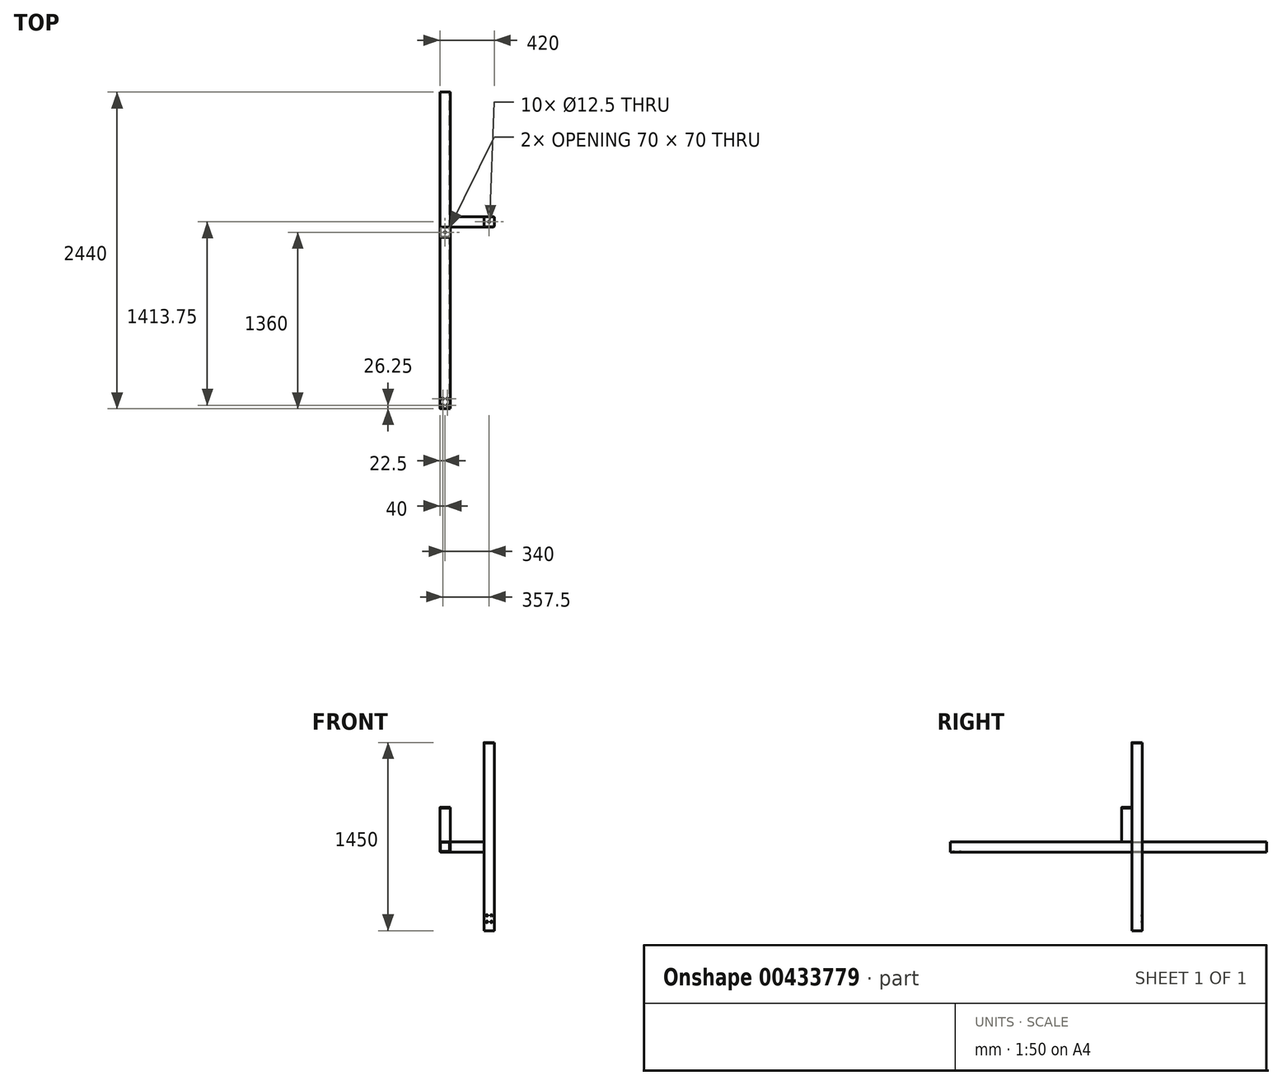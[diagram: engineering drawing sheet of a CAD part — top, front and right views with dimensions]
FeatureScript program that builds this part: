
annotation { "Feature Type Name" : "Feature", "Feature Type Description" : "" }
export const myFeature = defineFeature(function(context is Context, id is Id, definition is map)
    precondition{}
    {
        {
            var Q0;
            Q0=qCreatedBy(makeId("Top.planeOp"),FACE);
            var sketch = newSketch(context, id + "F0", { "sketchPlane" : qUnion([Q0])});
            skLineSegment(sketch, "E0.bottom", {"start": v(30, 40) * mm, "end": v(-30, 40) * mm});
            skLineSegment(sketch, "E0.top", {"start": v(30, -40) * mm, "end": v(-30, -40) * mm});
            skLineSegment(sketch, "E0.left", {"start": v(40, 30) * mm, "end": v(40, -30) * mm});
            skLineSegment(sketch, "E0.right", {"start": v(-40, 30) * mm, "end": v(-40, -30) * mm});
            skPoint(sketch, "E0.middle", {"position": v(0, 0) * mm});
            skPoint(sketch, "E1.visualSharp", {"position": v(-40, 40) * mm});
            skArc(sketch, "E1.filletArc", {"start": v(-30, 40) * mm, "mid": v(-37.07, 37.07) * mm, "end": v(-40, 30) * mm});
            skPoint(sketch, "E2.visualSharp", {"position": v(40, 40) * mm});
            skArc(sketch, "E2.filletArc", {"start": v(40, 30) * mm, "mid": v(37.07, 37.07) * mm, "end": v(30, 40) * mm});
            skPoint(sketch, "E3.visualSharp", {"position": v(40, -40) * mm});
            skArc(sketch, "E3.filletArc", {"start": v(30, -40) * mm, "mid": v(37.07, -37.07) * mm, "end": v(40, -30) * mm});
            skPoint(sketch, "E4.visualSharp", {"position": v(-40, -40) * mm});
            skArc(sketch, "E4.filletArc", {"start": v(-40, -30) * mm, "mid": v(-37.07, -37.07) * mm, "end": v(-30, -40) * mm});
            skArc(sketch, "E5.0", {"start": v(35, 30) * mm, "mid": v(33.54, 33.54) * mm, "end": v(30, 35) * mm});
            skLineSegment(sketch, "E5.1", {"start": v(35, 30) * mm, "end": v(35, -30) * mm});
            skLineSegment(sketch, "E5.2", {"start": v(30, 35) * mm, "end": v(-30, 35) * mm});
            skArc(sketch, "E5.3", {"start": v(30, -35) * mm, "mid": v(33.54, -33.54) * mm, "end": v(35, -30) * mm});
            skArc(sketch, "E5.4", {"start": v(-30, 35) * mm, "mid": v(-33.54, 33.54) * mm, "end": v(-35, 30) * mm});
            skLineSegment(sketch, "E5.5", {"start": v(-35, 30) * mm, "end": v(-35, -30) * mm});
            skArc(sketch, "E5.6", {"start": v(-35, -30) * mm, "mid": v(-33.54, -33.54) * mm, "end": v(-30, -35) * mm});
            skLineSegment(sketch, "E5.7", {"start": v(30, -35) * mm, "end": v(-30, -35) * mm});
            skSolve(sketch);
        }
        {
            var Q0;
            Q0=makeQuery(id+"F0.imprint","IMPRINT",FACE,{"disambiguationData":[TD([[makeQuery(id+"F0.imprint","IMPRINT",EDGE,{"derivedFrom":sQuery(id+"F0.wireOp",EDGE,"E0.bottom")}),1.0]])]});
            var Q1;
            Q1 = qConstructionFilter(qBodyType(qCreatedBy(id + "F0" ,EDGE), BodyType.WIRE), ConstructionObject.NO);
            extrude(context, id + "F1", {"entities" : qUnion([Q0]), "surfaceEntities" : qUnion([Q1]), "depth" : 1445 * mm});
        }
        {
            var Q0;
            Q0=makeQuery(id+"F1.opExtrude","SWEPT_FACE",FACE,{"disambiguationData":[OSD([sQuery(id+"F0.wireOp",EDGE,"E0.right")])]});
            var sketch = newSketch(context, id + "F2", { "sketchPlane" : qUnion([Q0])});
            skLineSegment(sketch, "E6", {"start": v(0, 1445) * mm, "end": v(0, 0) * mm, "construction": true});
            skLineSegment(sketch, "E7.bottom", {"start": v(30, 685) * mm, "end": v(-30, 685) * mm});
            skLineSegment(sketch, "E7.top", {"start": v(30, 605) * mm, "end": v(-30, 605) * mm});
            skLineSegment(sketch, "E7.left", {"start": v(40, 675) * mm, "end": v(40, 615) * mm});
            skLineSegment(sketch, "E7.right", {"start": v(-40, 675) * mm, "end": v(-40, 615) * mm});
            skPoint(sketch, "E7.middle", {"position": v(0, 645) * mm});
            skPoint(sketch, "E8.visualSharp", {"position": v(-40, 685) * mm});
            skArc(sketch, "E8.filletArc", {"start": v(-30, 685) * mm, "mid": v(-37.07, 682.07) * mm, "end": v(-40, 675) * mm});
            skPoint(sketch, "E9.visualSharp", {"position": v(40, 685) * mm});
            skArc(sketch, "E9.filletArc", {"start": v(40, 675) * mm, "mid": v(37.07, 682.07) * mm, "end": v(30, 685) * mm});
            skPoint(sketch, "E10.visualSharp", {"position": v(40, 605) * mm});
            skArc(sketch, "E10.filletArc", {"start": v(30, 605) * mm, "mid": v(37.07, 607.93) * mm, "end": v(40, 615) * mm});
            skPoint(sketch, "E11.visualSharp", {"position": v(-40, 605) * mm});
            skArc(sketch, "E11.filletArc", {"start": v(-40, 615) * mm, "mid": v(-37.07, 607.93) * mm, "end": v(-30, 605) * mm});
            skArc(sketch, "E12.0", {"start": v(35, 675) * mm, "mid": v(33.54, 678.54) * mm, "end": v(30, 680) * mm});
            skLineSegment(sketch, "E12.1", {"start": v(35, 675) * mm, "end": v(35, 615) * mm});
            skLineSegment(sketch, "E12.2", {"start": v(30, 680) * mm, "end": v(-30, 680) * mm});
            skArc(sketch, "E12.3", {"start": v(30, 610) * mm, "mid": v(33.54, 611.46) * mm, "end": v(35, 615) * mm});
            skArc(sketch, "E12.4", {"start": v(-30, 680) * mm, "mid": v(-33.54, 678.54) * mm, "end": v(-35, 675) * mm});
            skLineSegment(sketch, "E12.5", {"start": v(-35, 675) * mm, "end": v(-35, 615) * mm});
            skArc(sketch, "E12.6", {"start": v(-35, 615) * mm, "mid": v(-33.54, 611.46) * mm, "end": v(-30, 610) * mm});
            skLineSegment(sketch, "E12.7", {"start": v(30, 610) * mm, "end": v(-30, 610) * mm});
            skSolve(sketch);
        }
        {
            var Q0;
            Q0 = qSketchRegion(id + "F2", true);
            extrude(context, id + "F3", {"entities" : qUnion([Q0]), "depth" : 260 * mm});
        }
        {
            var Q0;
            Q0=qCreatedBy(makeId("Front.planeOp"),FACE);
            var sketch = newSketch(context, id + "F4", { "sketchPlane" : qUnion([Q0])});
            skLineSegment(sketch, "E13.bottom", {"start": v(-370, 685) * mm, "end": v(-310, 685) * mm});
            skLineSegment(sketch, "E13.top", {"start": v(-370, 605) * mm, "end": v(-310, 605) * mm});
            skLineSegment(sketch, "E13.left", {"start": v(-380, 675) * mm, "end": v(-380, 615) * mm});
            skLineSegment(sketch, "E13.right", {"start": v(-300, 675) * mm, "end": v(-300, 615) * mm});
            skPoint(sketch, "E13.middle", {"position": v(-340, 645) * mm});
            skPoint(sketch, "E14.visualSharp", {"position": v(-300, 685) * mm});
            skArc(sketch, "E14.filletArc", {"start": v(-300, 675) * mm, "mid": v(-302.93, 682.07) * mm, "end": v(-310, 685) * mm});
            skPoint(sketch, "E15.visualSharp", {"position": v(-380, 685) * mm});
            skArc(sketch, "E15.filletArc", {"start": v(-370, 685) * mm, "mid": v(-377.07, 682.07) * mm, "end": v(-380, 675) * mm});
            skPoint(sketch, "E16.visualSharp", {"position": v(-380, 605) * mm});
            skArc(sketch, "E16.filletArc", {"start": v(-380, 615) * mm, "mid": v(-377.07, 607.93) * mm, "end": v(-370, 605) * mm});
            skPoint(sketch, "E17.visualSharp", {"position": v(-300, 605) * mm});
            skArc(sketch, "E17.filletArc", {"start": v(-310, 605) * mm, "mid": v(-302.93, 607.93) * mm, "end": v(-300, 615) * mm});
            skArc(sketch, "E18.0", {"start": v(-370, 680) * mm, "mid": v(-373.54, 678.54) * mm, "end": v(-375, 675) * mm});
            skLineSegment(sketch, "E18.1", {"start": v(-375, 675) * mm, "end": v(-375, 615) * mm});
            skLineSegment(sketch, "E18.2", {"start": v(-370, 680) * mm, "end": v(-310, 680) * mm});
            skArc(sketch, "E18.3", {"start": v(-375, 615) * mm, "mid": v(-373.54, 611.46) * mm, "end": v(-370, 610) * mm});
            skArc(sketch, "E18.4", {"start": v(-305, 675) * mm, "mid": v(-306.46, 678.54) * mm, "end": v(-310, 680) * mm});
            skLineSegment(sketch, "E18.5", {"start": v(-305, 675) * mm, "end": v(-305, 615) * mm});
            skArc(sketch, "E18.6", {"start": v(-310, 610) * mm, "mid": v(-306.46, 611.46) * mm, "end": v(-305, 615) * mm});
            skLineSegment(sketch, "E18.7", {"start": v(-370, 610) * mm, "end": v(-310, 610) * mm});
            skSolve(sketch);
        }
        {
            var Q0;
            Q0 = qSketchRegion(id + "F4", true);
            extrude(context, id + "F5", {"entities" : qUnion([Q0]), "depth" : 1440 * mm, "hasSecondDirection" : true, "secondDirectionOppositeDirection" : true, "secondDirectionDepth" : 1000 * mm});
        }
        {
            var Q0;
            Q0=makeQuery(id+"F5.opExtrude","SWEPT_FACE",FACE,{"disambiguationData":[OSD([sQuery(id+"F4.wireOp",EDGE,"E13.bottom")])]});
            var sketch = newSketch(context, id + "F6", { "sketchPlane" : qUnion([Q0])});
            skCircle(sketch, "E19", {"center": v(-322.5, -1413.75) * mm, "radius": 6.25 * mm});
            skCircle(sketch, "E20.0.1.0", {"center": v(-322.5, -1363.75) * mm, "radius": 6.25 * mm});
            skCircle(sketch, "E20.1.0.0", {"center": v(-357.5, -1413.75) * mm, "radius": 6.25 * mm});
            skCircle(sketch, "E20.1.1.0", {"center": v(-357.5, -1363.75) * mm, "radius": 6.25 * mm});
            skLineSegment(sketch, "E20.direction1", {"start": v(-322.5, -1413.75) * mm, "end": v(-357.5, -1413.75) * mm, "construction": true});
            skLineSegment(sketch, "E20.direction2", {"start": v(-322.5, -1413.75) * mm, "end": v(-322.5, -1363.75) * mm, "construction": true});
            skSolve(sketch);
        }
        {
            var Q0;
            Q0 = qSketchRegion(id + "F6", true);
            extrude(context, id + "F7", {"entities" : qUnion([Q0]), "operationType" : NewBodyOperationType.REMOVE, "endBound" : BoundingType.THROUGH_ALL, "oppositeDirection" : true, "depth" : 25 * mm});
        }
        {
            var Q0;
            Q0=makeQuery(id+"F1.opExtrude","SWEPT_FACE",FACE,{"disambiguationData":[OSD([sQuery(id+"F0.wireOp",EDGE,"E0.top")])]});
            var sketch = newSketch(context, id + "F8", { "sketchPlane" : qUnion([Q0])});
            skLineSegment(sketch, "E21", {"start": v(0, 0) * mm, "end": v(0, 38.96) * mm, "construction": true});
            skCircle(sketch, "E22", {"center": v(17.5, 117.5) * mm, "radius": 6.25 * mm});
            skCircle(sketch, "E23", {"center": v(17.5, 67.5) * mm, "radius": 6.25 * mm});
            skCircle(sketch, "E24.MirrorC", {"center": v(-17.5, 67.5) * mm, "radius": 6.25 * mm});
            skCircle(sketch, "E25.MirrorC", {"center": v(-17.5, 117.5) * mm, "radius": 6.25 * mm});
            skSolve(sketch);
        }
        {
            var Q0;
            Q0 = qSketchRegion(id + "F8", true);
            extrude(context, id + "F9", {"entities" : qUnion([Q0]), "operationType" : NewBodyOperationType.REMOVE, "endBound" : BoundingType.THROUGH_ALL, "oppositeDirection" : true, "depth" : 25 * mm});
        }
        {
            var Q0;
            Q0=makeQuery(id+"F1.opExtrude","CAP_FACE",FACE,{"disambiguationData":[OSD([sQuery(id+"F0.wireOp",EDGE,"E0.bottom"),sQuery(id+"F0.wireOp",EDGE,"E0.top"),sQuery(id+"F0.wireOp",EDGE,"E0.left"),sQuery(id+"F0.wireOp",EDGE,"E0.right"),sQuery(id+"F0.wireOp",EDGE,"E1.filletArc"),sQuery(id+"F0.wireOp",EDGE,"E2.filletArc"),sQuery(id+"F0.wireOp",EDGE,"E3.filletArc"),sQuery(id+"F0.wireOp",EDGE,"E4.filletArc"),sQuery(id+"F0.wireOp",EDGE,"E5.0"),sQuery(id+"F0.wireOp",EDGE,"E5.1"),sQuery(id+"F0.wireOp",EDGE,"E5.2"),sQuery(id+"F0.wireOp",EDGE,"E5.3"),sQuery(id+"F0.wireOp",EDGE,"E5.4"),sQuery(id+"F0.wireOp",EDGE,"E5.5"),sQuery(id+"F0.wireOp",EDGE,"E5.6"),sQuery(id+"F0.wireOp",EDGE,"E5.7")])],"isStart":false});
            var sketch = newSketch(context, id + "F10", { "sketchPlane" : qUnion([Q0])});
            skLineSegment(sketch, "E26.0", {"start": v(30, 40) * mm, "end": v(-30, 40) * mm});
            skArc(sketch, "E26.1", {"start": v(40, 30) * mm, "mid": v(37.07, 37.07) * mm, "end": v(30, 40) * mm});
            skLineSegment(sketch, "E26.2", {"start": v(40, 30) * mm, "end": v(40, -30) * mm});
            skArc(sketch, "E26.3", {"start": v(30, -40) * mm, "mid": v(37.07, -37.07) * mm, "end": v(40, -30) * mm});
            skLineSegment(sketch, "E26.4", {"start": v(30, -40) * mm, "end": v(-30, -40) * mm});
            skArc(sketch, "E26.5", {"start": v(-40, -30) * mm, "mid": v(-37.07, -37.07) * mm, "end": v(-30, -40) * mm});
            skLineSegment(sketch, "E26.6", {"start": v(-40, 30) * mm, "end": v(-40, -30) * mm});
            skArc(sketch, "E26.7", {"start": v(-30, 40) * mm, "mid": v(-37.07, 37.07) * mm, "end": v(-40, 30) * mm});
            skCircle(sketch, "E27", {"center": v(0, 0) * mm, "radius": 6.25 * mm});
            skSolve(sketch);
        }
        {
            var Q0;
            Q0 = qSketchRegion(id + "F10", true);
            extrude(context, id + "F11", {"entities" : qUnion([Q0]), "depth" : 5 * mm});
        }
        {
            var Q0;
            Q0=makeQuery(id+"F5.opExtrude","SWEPT_FACE",FACE,{"disambiguationData":[OSD([sQuery(id+"F4.wireOp",EDGE,"E13.bottom")])]});
            var sketch = newSketch(context, id + "F12", { "sketchPlane" : qUnion([Q0])});
            skLineSegment(sketch, "E28.bottom", {"start": v(-310, -40) * mm, "end": v(-370, -40) * mm});
            skLineSegment(sketch, "E28.top", {"start": v(-310, -120) * mm, "end": v(-370, -120) * mm});
            skLineSegment(sketch, "E28.left", {"start": v(-300, -50) * mm, "end": v(-300, -110) * mm});
            skLineSegment(sketch, "E28.right", {"start": v(-380, -50) * mm, "end": v(-380, -110) * mm});
            skPoint(sketch, "E28.middle", {"position": v(-340, -80) * mm});
            skPoint(sketch, "E29.visualSharp", {"position": v(-380, -40) * mm});
            skArc(sketch, "E29.filletArc", {"start": v(-370, -40) * mm, "mid": v(-377.07, -42.93) * mm, "end": v(-380, -50) * mm});
            skPoint(sketch, "E30.visualSharp", {"position": v(-300, -40) * mm});
            skArc(sketch, "E30.filletArc", {"start": v(-300, -50) * mm, "mid": v(-302.93, -42.93) * mm, "end": v(-310, -40) * mm});
            skPoint(sketch, "E31.visualSharp", {"position": v(-300, -120) * mm});
            skArc(sketch, "E31.filletArc", {"start": v(-310, -120) * mm, "mid": v(-302.93, -117.07) * mm, "end": v(-300, -110) * mm});
            skPoint(sketch, "E32.visualSharp", {"position": v(-380, -120) * mm});
            skArc(sketch, "E32.filletArc", {"start": v(-380, -110) * mm, "mid": v(-377.07, -117.07) * mm, "end": v(-370, -120) * mm});
            skLineSegment(sketch, "E33.0", {"start": v(-310, -45) * mm, "end": v(-370, -45) * mm});
            skArc(sketch, "E33.1", {"start": v(-305, -50) * mm, "mid": v(-306.46, -46.46) * mm, "end": v(-310, -45) * mm});
            skArc(sketch, "E33.2", {"start": v(-370, -45) * mm, "mid": v(-373.54, -46.46) * mm, "end": v(-375, -50) * mm});
            skLineSegment(sketch, "E33.3", {"start": v(-305, -50) * mm, "end": v(-305, -110) * mm});
            skLineSegment(sketch, "E33.4", {"start": v(-375, -50) * mm, "end": v(-375, -110) * mm});
            skArc(sketch, "E33.5", {"start": v(-375, -110) * mm, "mid": v(-373.54, -113.54) * mm, "end": v(-370, -115) * mm});
            skLineSegment(sketch, "E33.6", {"start": v(-310, -115) * mm, "end": v(-370, -115) * mm});
            skArc(sketch, "E33.7", {"start": v(-310, -115) * mm, "mid": v(-306.46, -113.54) * mm, "end": v(-305, -110) * mm});
            skSolve(sketch);
        }
        {
            var Q0;
            Q0 = qSketchRegion(id + "F12", true);
            extrude(context, id + "F13", {"entities" : qUnion([Q0]), "depth" : 260 * mm});
        }
        {
            var Q0;
            Q0=makeQuery(id+"F13.opExtrude","CAP_FACE",FACE,{"disambiguationData":[OSD([sQuery(id+"F12.wireOp",EDGE,"E28.bottom"),sQuery(id+"F12.wireOp",EDGE,"E28.top"),sQuery(id+"F12.wireOp",EDGE,"E28.left"),sQuery(id+"F12.wireOp",EDGE,"E28.right"),sQuery(id+"F12.wireOp",EDGE,"E29.filletArc"),sQuery(id+"F12.wireOp",EDGE,"E30.filletArc"),sQuery(id+"F12.wireOp",EDGE,"E31.filletArc"),sQuery(id+"F12.wireOp",EDGE,"E32.filletArc"),sQuery(id+"F12.wireOp",EDGE,"E33.0"),sQuery(id+"F12.wireOp",EDGE,"E33.1"),sQuery(id+"F12.wireOp",EDGE,"E33.2"),sQuery(id+"F12.wireOp",EDGE,"E33.3"),sQuery(id+"F12.wireOp",EDGE,"E33.4"),sQuery(id+"F12.wireOp",EDGE,"E33.5"),sQuery(id+"F12.wireOp",EDGE,"E33.6"),sQuery(id+"F12.wireOp",EDGE,"E33.7")])],"isStart":false});
            var sketch = newSketch(context, id + "F14", { "sketchPlane" : qUnion([Q0])});
            skLineSegment(sketch, "E34.0", {"start": v(-310, -40) * mm, "end": v(-370, -40) * mm});
            skArc(sketch, "E34.1", {"start": v(-370, -40) * mm, "mid": v(-377.07, -42.93) * mm, "end": v(-380, -50) * mm});
            skLineSegment(sketch, "E34.2", {"start": v(-380, -50) * mm, "end": v(-380, -110) * mm});
            skArc(sketch, "E34.3", {"start": v(-300, -50) * mm, "mid": v(-302.93, -42.93) * mm, "end": v(-310, -40) * mm});
            skLineSegment(sketch, "E34.4", {"start": v(-300, -50) * mm, "end": v(-300, -110) * mm});
            skArc(sketch, "E34.5", {"start": v(-310, -120) * mm, "mid": v(-302.93, -117.07) * mm, "end": v(-300, -110) * mm});
            skLineSegment(sketch, "E34.6", {"start": v(-310, -120) * mm, "end": v(-370, -120) * mm});
            skArc(sketch, "E34.7", {"start": v(-380, -110) * mm, "mid": v(-377.07, -117.07) * mm, "end": v(-370, -120) * mm});
            skCircle(sketch, "E35", {"center": v(-340, -80) * mm, "radius": 6.25 * mm});
            skPoint(sketch, "E35.centerSnap0", {"position": v(-305, -80) * mm});
            skPoint(sketch, "E35.centerSnap1", {"position": v(-340, -45) * mm});
            skSolve(sketch);
        }
        {
            var Q0;
            Q0 = qSketchRegion(id + "F14", true);
            extrude(context, id + "F15", {"entities" : qUnion([Q0]), "depth" : 5 * mm});
        }
    });
